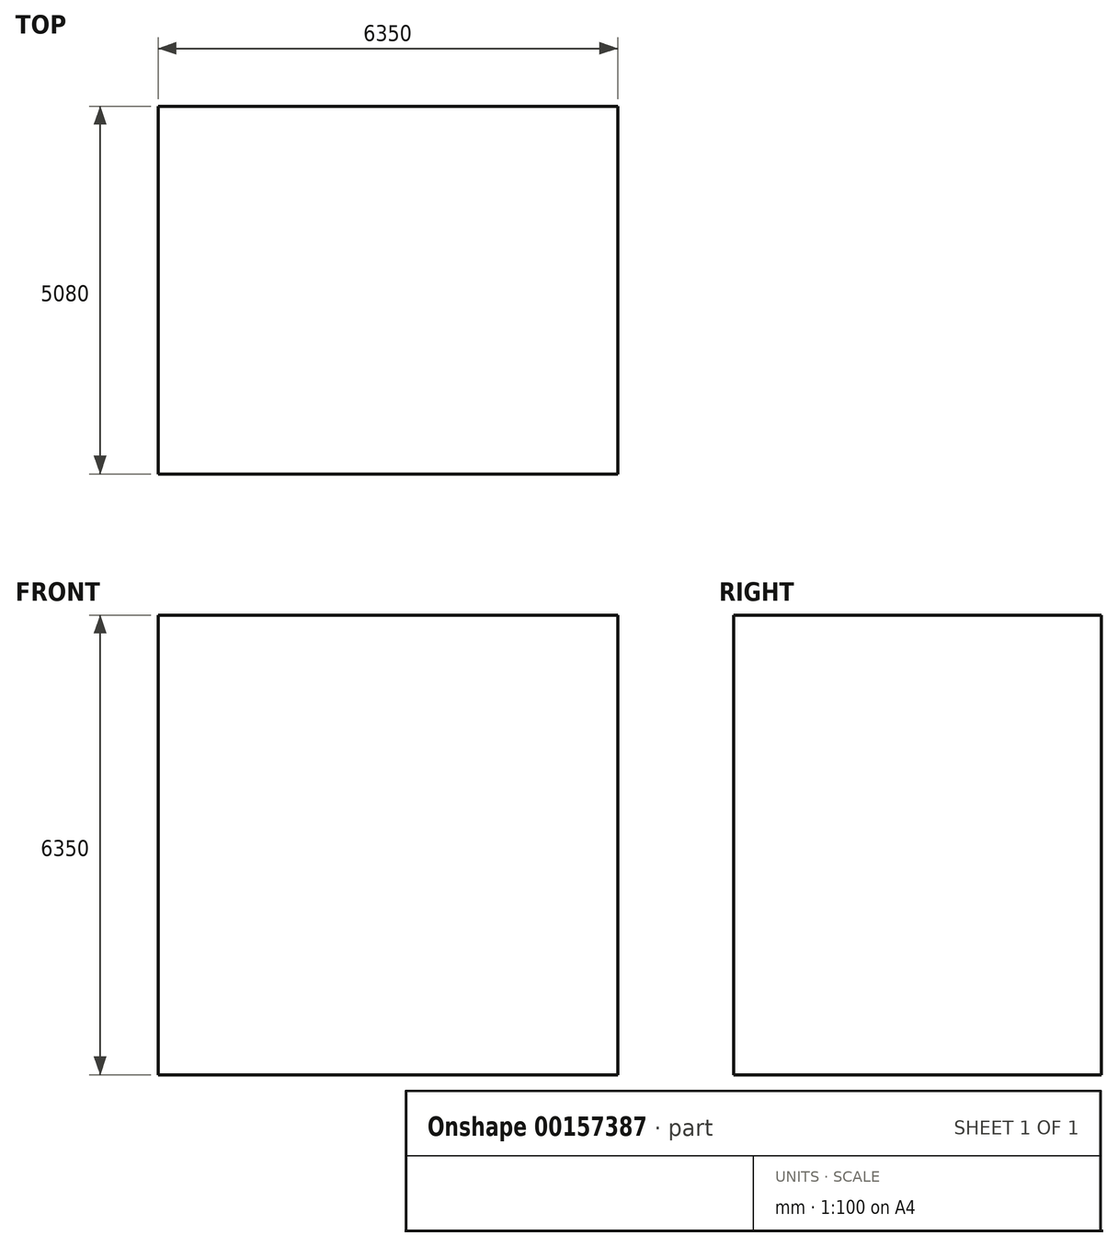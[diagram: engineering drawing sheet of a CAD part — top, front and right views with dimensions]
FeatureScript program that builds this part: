
annotation { "Feature Type Name" : "Feature", "Feature Type Description" : "" }
export const myFeature = defineFeature(function(context is Context, id is Id, definition is map)
    precondition{}
    {
        {
            var Q0;
            Q0=qCreatedBy(makeId("Front.planeOp"),FACE);
            var sketch = newSketch(context, id + "F0", { "sketchPlane" : qUnion([Q0])});
            skLineSegment(sketch, "E0.bottom", {"start": v(-56.43, 6301) * mm, "end": v(6293.57, 6301) * mm});
            skLineSegment(sketch, "E0.top", {"start": v(-56.43, -49) * mm, "end": v(6293.57, -49) * mm});
            skLineSegment(sketch, "E0.left", {"start": v(-56.43, 6301) * mm, "end": v(-56.43, -49) * mm});
            skLineSegment(sketch, "E0.right", {"start": v(6293.57, 6301) * mm, "end": v(6293.57, -49) * mm});
            skSolve(sketch);
        }
        {
            var Q0;
            Q0=makeQuery(id+"F0.imprint","IMPRINT",FACE,{"disambiguationData":[TD([[makeQuery(id+"F0.imprint","IMPRINT",EDGE,{"derivedFrom":sQuery(id+"F0.wireOp",EDGE,"E0.bottom")}),-1.0]])]});
            extrude(context, id + "F1", {"entities" : qUnion([Q0]), "depth" : 2540 * mm, "hasSecondDirection" : true, "secondDirectionOppositeDirection" : true, "secondDirectionDepth" : 2540 * mm});
        }
    });
